# Revit family: 3116512D_3116512DC_NE-MAST 12.0M Ø89 RO240 EUROSKJØT
name_source: partatom
category: Lighting Fixtures
units: mm (PartAtom-declared; Revit-internal decimal feet)

## family parameters
Always vertical = Yes
Cut with Voids When Loaded = No
Light Source = No
Maintain Annotation Orientation = No
OmniClass Number = 23.80.70.14.21
OmniClass Title = Street and Roadway Lighting
Part Type = Normal
Room Calculation Point = No
Round Connector Dimension = Use Diameter
Shared = No
Work Plane-Based = No

## types (1)
- Ettergivende master NE
    Area = 9,88 m²
    Art.nr = 3116512D/3116512DC
    Art.nr CombiCoat = 3116512DC
    Art.nr VZN = 3116512D
    Bunndiameter = Ø168
    CE-godkjent = Ja
    Category = Ettergivende master NE
    Center of Gravity = X: -0,002 mm Y: 1,010 mm Z: 4653,012 mm
    Default Elevation = 0 mm  [stored 0 ft]
    Density = 7810,06 kg/m³
    Description = NE-MAST 12.0M Ø89 RO240 EUROSKJØT
    Design Status = 1
    Designer = khk
    EL nr CombiCoat = 3641056
    El nr = 3640106/3640118
    El nr VZN = 3641050
    Filnamn-VO = Standard
    Filnavn = NE-MAST 12.0M Ø89 RO240 EUROSKJØT
    Fotplate C/C bolter = RO240
    Fundament = Fotplate
    Lyspunkthoyde = 12m
    Manufacturer = Vik Ørsta AS
    Mass = 157,33 kg
    Model = 3116512D_3116512DC
    Part Number = L10364
    Requested Accuracy = Low
    Revision Number = -
    Size = 0,0,0
    Sti&Filnamn-VO = Standard
    Title = NE-MAST 12.0M Ø89 RO240 EUROSKJØT
    Toppdiameter = Ø89
    Volume = 0,02 m³

note: [stored X ft] marks values corroborated as IEEE doubles in the binary element streams (Revit-internal decimal feet)

## geometry (parser evidence)
native form markers: Sweep x3
no freeform markers — native parametric forms only
